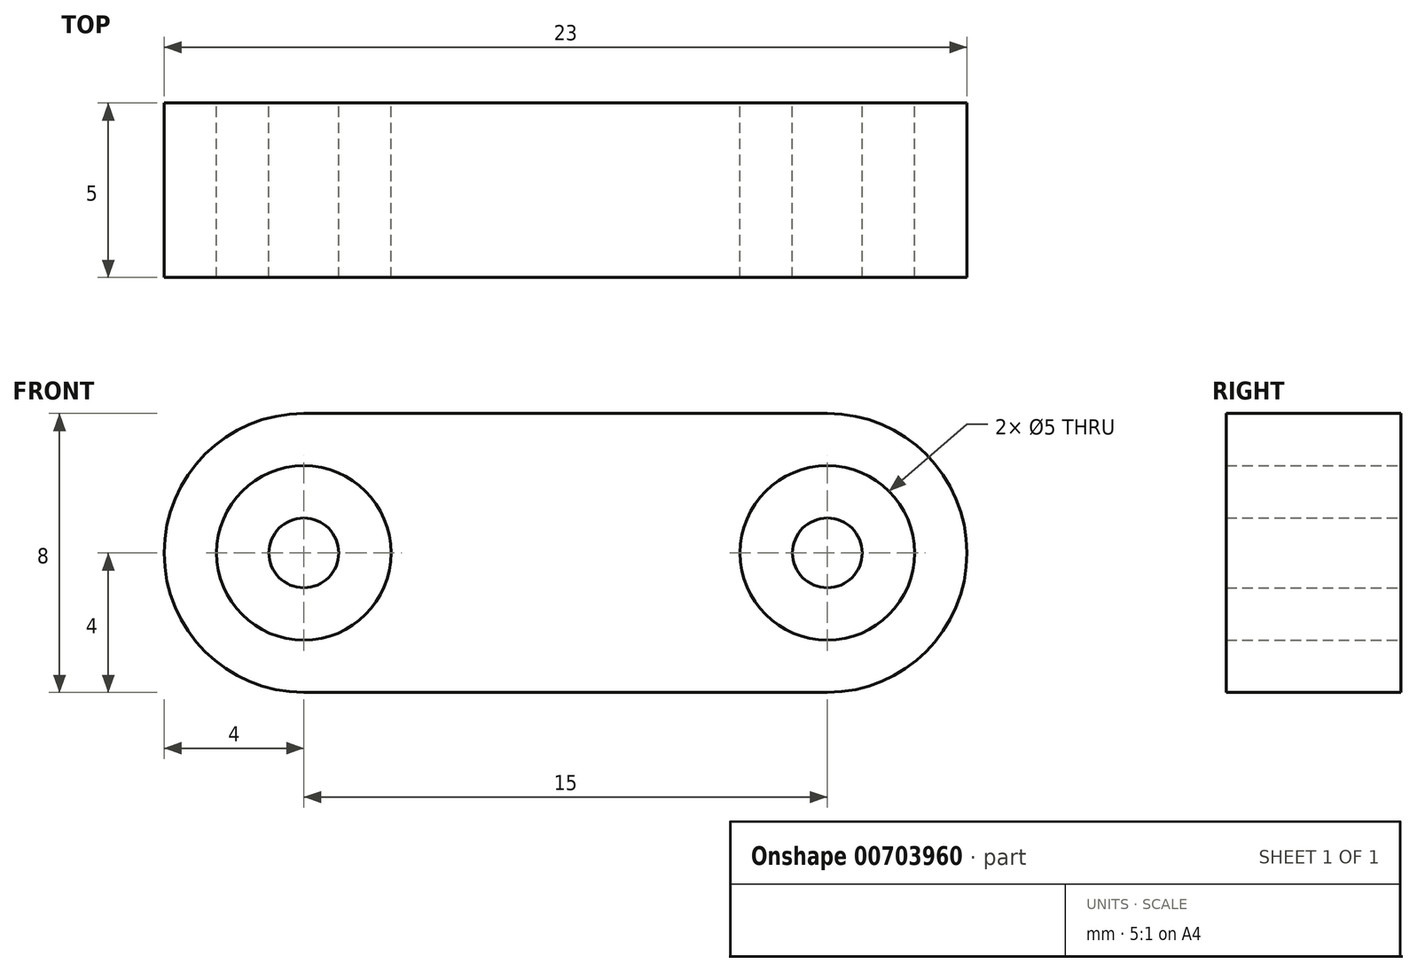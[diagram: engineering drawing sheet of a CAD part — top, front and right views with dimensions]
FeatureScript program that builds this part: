
annotation { "Feature Type Name" : "Feature", "Feature Type Description" : "" }
export const myFeature = defineFeature(function(context is Context, id is Id, definition is map)
    precondition{}
    {
        {
            var Q0;
            Q0=qCreatedBy(makeId("Front.planeOp"),FACE);
            var sketch = newSketch(context, id + "F0", { "sketchPlane" : qUnion([Q0])});
            skLineSegment(sketch, "E0.bottom", {"start": v(0, 0) * mm, "end": v(15, 0) * mm});
            skLineSegment(sketch, "E0.top", {"start": v(0, 8) * mm, "end": v(15, 8) * mm});
            skArc(sketch, "E1", {"start": v(15, 0) * mm, "mid": v(19, 4) * mm, "end": v(15, 8) * mm});
            skArc(sketch, "E2", {"start": v(0, 8) * mm, "mid": v(-4, 4) * mm, "end": v(0, 0) * mm});
            skCircle(sketch, "E3", {"center": v(0, 4) * mm, "radius": 2.5 * mm});
            skCircle(sketch, "E4", {"center": v(15, 4) * mm, "radius": 2.5 * mm});
            skCircle(sketch, "E5", {"center": v(15, 4) * mm, "radius": 1 * mm});
            skCircle(sketch, "E6", {"center": v(0, 4) * mm, "radius": 1 * mm});
            skSolve(sketch);
        }
        {
            var Q0;
            Q0 = qSketchRegion(id + "F0", true);
            var Q1;
            Q1=makeQuery(id+"F0.imprint","IMPRINT",FACE,{"disambiguationData":[TD([[makeQuery(id+"F0.imprint","IMPRINT",EDGE,{"derivedFrom":sQuery(id+"F0.wireOp",EDGE,"E6")}),1.0]])]});
            var Q2;
            Q2=makeQuery(id+"F0.imprint","IMPRINT",FACE,{"disambiguationData":[TD([[makeQuery(id+"F0.imprint","IMPRINT",EDGE,{"derivedFrom":sQuery(id+"F0.wireOp",EDGE,"E5")}),1.0]])]});
            extrude(context, id + "F1", {"entities" : qUnion([Q0, Q1, Q2]), "depth" : 5 * mm, "offsetDistance" : 25 * mm});
        }
    });
